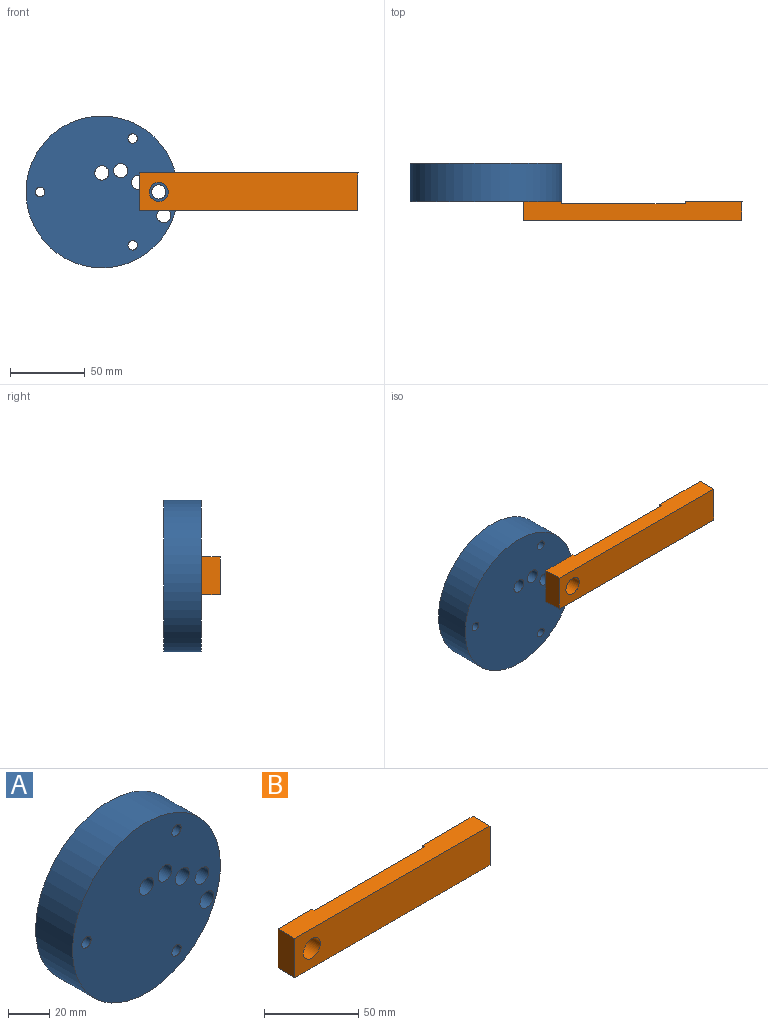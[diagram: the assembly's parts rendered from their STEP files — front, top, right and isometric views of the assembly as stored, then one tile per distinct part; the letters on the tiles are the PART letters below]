
ASSEMBLY  parts=2 mates=1
PART A: 11 faces, bbox 101.6x25.4x101.6 mm
  f0: cylinder r=4.76mm len=25.4mm, axis (0,1,0), area 760.1mm2, adj f6,f7
  f1: cylinder r=4.76mm len=25.4mm, axis (0,1,0), area 760.1mm2, adj f6,f7
  f2: cylinder r=4.76mm len=25.4mm, axis (0,1,0), area 760.1mm2, adj f6,f7
  f3: cylinder r=4.76mm len=25.4mm, axis (0,1,0), area 760.1mm2, adj f6,f7
  f4: cylinder r=4.76mm len=25.4mm, axis (0,1,0), area 760.1mm2, adj f6,f7
  f5: cylinder r=50.8mm len=101.6mm, axis (0,1,0), area 8107.3mm2, adj f6,f7
  f6: plane 101.6x101.6mm, normal (0,-1,0), area 7656mm2, adj f0,f1,f2,f3,f4,f5,f8,f9
  f7: plane 101.6x101.6mm, normal (0,1,0), area 7656mm2, adj f0,f1,f2,f3,f4,f5,f8,f9
  f8: cylinder r=3.17mm len=25.4mm, axis (0,1,0), area 506.7mm2, adj f6,f7
  f9: cylinder r=3.17mm len=25.4mm, axis (0,1,0), area 506.7mm2, adj f6,f7
  f10: cylinder r=3.17mm len=25.4mm, axis (0,1,0), area 506.7mm2, adj f6,f7
PART B: 13 faces, bbox 146.1x12.7x25.4 mm
  f0: plane 146.05x12.7mm, normal (0,0,1), area 1724.8mm2, adj f2,f3,f5,f6,f7,f8,f9,f10
  f1: plane 146.05x12.7mm, normal (0,0,-1), area 1724.8mm2, adj f2,f3,f5,f6,f7,f8,f9,f10
  f2: plane 38.1x25.4mm, normal (0,1,0), area 967.7mm2, adj f0,f1,f5,f10
  f3: plane 25.4x12.7mm, normal (-1,0,0), area 322.6mm2, adj f0,f1,f6,f7
  f4: cylinder r=6.35mm len=12.7mm, axis (0,1,0), area 506.7mm2, adj f6,f7
  f5: plane 25.4x12.7mm, normal (1,0,0), area 273.3mm2, adj f0,f1,f2,f6,f11
  f6: plane 146.05x25.4mm, normal (0,-1,0), area 3583mm2, adj f0,f1,f3,f4,f5
  f7: plane 25.4x25.4mm, normal (0,1,0), area 518.5mm2, adj f0,f1,f3,f4,f8
  f8: plane 25.4x1.57mm, normal (1,0,0), area 40mm2, adj f0,f1,f7,f9
  f9: plane 82.55x25.4mm, normal (0,1,0), area 2096.8mm2, adj f0,f1,f8,f10
  f10: plane 25.4x1.57mm, normal (-1,0,0), area 40mm2, adj f0,f1,f2,f9
  f11: cylinder r=3.96mm len=73.03mm, axis (-1,0,0), area 1818.1mm2, adj f5,f12
  f12: plane 7.92x7.92mm, normal (1,0,0), area 49.3mm2, adj f11
PLACE A rot(axis=(0.99,0.02,-0.1),0deg) t=(-43.56,3.03,64.28)mm
PLACE B rot(axis=(0.92,0.39,-0.09),0deg) t=(54.86,-22.37,64.28)mm
MATE revolute A.f3 <-> B.f4  axis (0,1,0) through (-5.46,-22.37,64.28)mm
